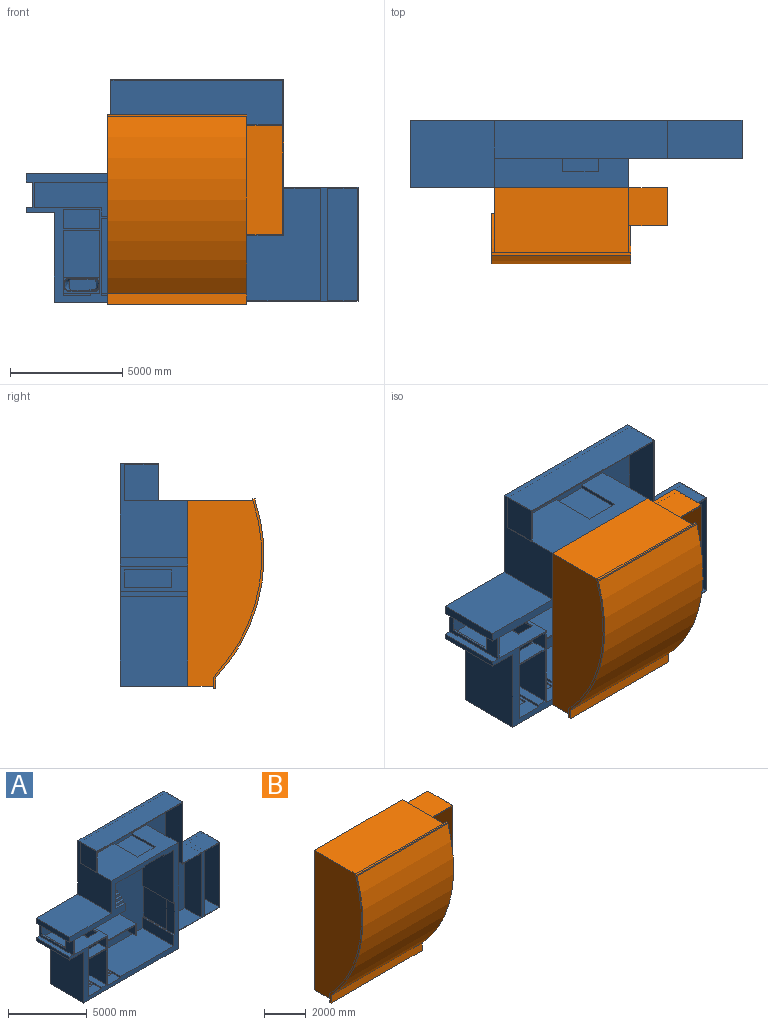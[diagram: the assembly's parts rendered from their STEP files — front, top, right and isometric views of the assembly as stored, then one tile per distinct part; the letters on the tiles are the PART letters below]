
ASSEMBLY  parts=2 mates=1
PART A: 183 faces, bbox 14773.6x3003.6x9893.6 mm
  f0: plane 2020x1630mm, normal (0,0,1), area 1096600mm2, adj f4,f10,f11,f13,f82,f112
  f1: cylinder r=5mm len=1630mm, axis (1,0,0), area 12802mm2, adj f4,f7,f11,f112
  f2: bspline ~1510x560mm, area 1818583mm2, adj f3,f5
  f3: plane 1220x470mm, normal (0,-1,0), area 564814mm2, adj f2
  f4: plane 1633.58x698.58mm, normal (0,-1,0), area 248006.1mm2, adj f0,f1,f5,f11,f112
  f5: bspline ~1556.23x596.37mm, area 160277.6mm2, adj f2,f4
  f6: plane 3000x400mm, normal (-1,0,0), area 1200000mm2, adj f13,f47,f56,f57
  f7: plane 1630x775mm, normal (0,0,1), area 1263250mm2, adj f1,f11,f27,f112
  f8: plane 1800x1220mm, normal (0,0,1), area 1096000mm2, adj f9,f13,f25,f73,f74,f75,f77
  f9: plane 1800x100mm, normal (-1,0,0), area 180000mm2, adj f8,f13,f26,f74
  f10: plane 1800x100mm, normal (-1,0,0), area 180000mm2, adj f0,f13,f39,f82
  f11: plane 2800x2790mm, normal (-1,0,0), area 7266005.4mm2, adj f0,f1,f4,f7,f12,f13,f27
  f12: plane 2800x1630mm, normal (0,0,-1), area 2674000mm2, adj f11,f13,f27,f88,f90,f91,f112
  f13: plane 9730x8240mm, normal (0,-1,0), area 13790385mm2, adj f0,f6,f8,f9,f10,f11,f12,f14
  f14: plane 2800x870mm, normal (1,0,0), area 2436000mm2, adj f13,f27,f40,f48
  f15: plane 4600x2800mm, normal (0,0,-1), area 10751500mm2, adj f13,f16,f17,f27,f113,f155
  f16: plane 2800x1130mm, normal (1,0,0), area 1484000mm2, adj f13,f15,f18,f27,f95,f96,f97
  f17: plane 2510x2475mm, normal (1,0,0), area 4446718.8mm2, adj f15,f27,f41,f139,f155,f156,f157,f158
  f18: plane 2970x2800mm, normal (0,0,1), area 6426000mm2, adj f13,f16,f19,f27,f92,f93,f94
  f19: plane 2800x400mm, normal (1,0,0), area 1120000mm2, adj f13,f18,f20,f27
  f20: plane 2800x2600mm, normal (0,0,1), area 7280000mm2, adj f13,f19,f21,f27
  f21: plane 2800x870mm, normal (1,0,0), area 2436000mm2, adj f13,f20,f22,f27
  f22: plane 2800x80mm, normal (0,0,-1), area 224000mm2, adj f13,f21,f23,f27
  f23: plane 2800x800mm, normal (-1,0,0), area 2240000mm2, adj f13,f22,f24,f27
  f24: plane 2800x2520mm, normal (0,0,-1), area 7056000mm2, adj f13,f23,f25,f27
  f25: plane 3430x2800mm, normal (1,0,0), area 9504000mm2, adj f8,f13,f24,f26,f27,f74
  f26: plane 5960x2800mm, normal (0,0,1), area 14492000mm2, adj f9,f13,f25,f27,f28,f74
  f27: plane 9131x7541mm, normal (0,-1,0), area 50748600mm2, adj f7,f11,f12,f14,f15,f16,f17,f18
  f28: plane 2800x840mm, normal (-1,0,0), area 2352000mm2, adj f13,f26,f27,f29
  f29: plane 2800x100mm, normal (0,0,1), area 280000mm2, adj f13,f27,f28,f31
  f30: plane 2800x100mm, normal (0,0,-1), area 280000mm2, adj f13,f27,f31,f34
  f31: plane 2800x2470mm, normal (-1,0,0), area 1876000mm2, adj f13,f27,f29,f30,f55,f115,f117
  f32: plane 5990x2800mm, normal (0,0,1), area 13352000mm2, adj f13,f33,f54,f58,f64,f65,f66,f68
  f33: plane 8240x3000mm, normal (1,0,0), area 17978000mm2, adj f13,f32,f53,f57,f63,f64,f71,f99
  f34: plane 4130x2800mm, normal (-1,0,0), area 11564000mm2, adj f13,f27,f30,f35
  f35: plane 2800x890mm, normal (0,0,-1), area 2492000mm2, adj f13,f27,f34,f36
  f36: plane 2800x100mm, normal (-1,0,0), area 280000mm2, adj f13,f27,f35,f38
  f37: plane 2800x100mm, normal (1,0,0), area 280000mm2, adj f13,f27,f38,f44
  f38: plane 2800x1720mm, normal (0,0,-1), area 1456000mm2, adj f13,f27,f36,f37,f69,f70,f72
  f39: plane 1800x1220mm, normal (0,0,1), area 1096000mm2, adj f10,f13,f81,f82,f84,f85,f112
  f40: plane 2800x1630mm, normal (0,0,1), area 2674000mm2, adj f13,f14,f27,f88,f90,f91,f111
  f41: plane 1818.75x1250mm, normal (0,0,-1), area 1791093.8mm2, adj f17,f27,f125,f127,f128,f129,f130,f131
  f42: plane 1100x75mm, normal (1,0,0), area 82500mm2, adj f53,f76,f80,f122
  f43: plane 1400x1240mm, normal (0,0,-1), area 376781.2mm2, adj f27,f113,f124,f125,f127,f128,f129,f130
  f44: plane 2800x2580mm, normal (0,0,-1), area 4927125mm2, adj f13,f27,f37,f46,f124,f140,f141,f142
  f45: plane 3000x1130mm, normal (-1,0,0), area 1710000mm2, adj f13,f27,f47,f49,f57,f95,f96,f97
  f46: plane 1946.25x1400mm, normal (1,0,0), area 1922375mm2, adj f13,f44,f126,f140,f169,f170,f171,f172
  f47: plane 3000x300mm, normal (0,0,-1), area 900000mm2, adj f6,f13,f45,f57
  f48: plane 2800x1630mm, normal (0,0,-1), area 2674000mm2, adj f13,f14,f27,f92,f93,f94,f111
  f49: plane 3000x300mm, normal (0,0,1), area 900000mm2, adj f13,f45,f50,f57
  f50: plane 3000x236mm, normal (-1,0,0), area 708000mm2, adj f13,f49,f51,f57
  f51: plane 3000x1260mm, normal (0,0,-1), area 3780000mm2, adj f13,f50,f52,f57
  f52: plane 3964x3000mm, normal (-1,0,0), area 11892000mm2, adj f13,f51,f53,f57
  f53: plane 8470x3000mm, normal (0,0,-1), area 23210000mm2, adj f13,f33,f42,f52,f57,f76,f79,f80
  f54: plane 4160x3000mm, normal (-1,0,0), area 7860000mm2, adj f13,f32,f56,f57,f58,f59
  f55: plane 2400x1mm, normal (0,1,0), area 2400mm2, adj f31,f78,f115,f117
  f56: plane 3740x3000mm, normal (0,0,1), area 11220000mm2, adj f6,f13,f54,f57
  f57: plane 14770x9890mm, normal (0,1,0), area 109210260mm2, adj f6,f33,f45,f47,f49,f50,f51,f52
  f58: plane 1650x1mm, normal (0,-1,0), area 1650mm2, adj f32,f54,f59,f110
  f59: plane 7720x1700mm, normal (0,0,1), area 13122500mm2, adj f54,f57,f58,f60,f99,f110
  f60: plane 4780x1700mm, normal (1,0,0), area 8126000mm2, adj f57,f59,f61,f99
  f61: plane 3310x1700mm, normal (0,0,1), area 5627000mm2, adj f57,f60,f62,f99
  f62: plane 5080x1700mm, normal (1,0,0), area 8636000mm2, adj f57,f61,f63,f99
  f63: plane 5040x1700mm, normal (0,0,-1), area 8568000mm2, adj f33,f57,f62,f99
  f64: plane 9780x9329mm, normal (0,-1,0), area 35156090mm2, adj f32,f33,f65,f67,f68,f71,f103,f105
  f65: plane 2100x150mm, normal (1,0,0), area 315000mm2, adj f32,f64,f66,f67
  f66: plane 1600x150mm, normal (0,1,0), area 240000mm2, adj f32,f65,f67,f68
  f67: plane 2100x1600mm, normal (0,0,1), area 3360000mm2, adj f64,f65,f66,f68
  f68: plane 2100x150mm, normal (-1,0,0), area 315000mm2, adj f32,f64,f66,f67
  f69: plane 2100x1mm, normal (-1,0,0), area 2100mm2, adj f27,f38,f72,f118
  f70: plane 2100x1mm, normal (1,0,0), area 2100mm2, adj f27,f38,f72,f118
  f71: plane 2100x150mm, normal (0,0,1), area 315000mm2, adj f33,f64,f114,f119
  f72: plane 1600x1mm, normal (0,1,0), area 1600mm2, adj f38,f69,f70,f118
  f73: plane 1000x75mm, normal (0,1,0), area 75000mm2, adj f8,f75,f77,f121
  f74: plane 1220x175mm, normal (0,-1,0), area 197000mm2, adj f8,f9,f25,f26,f75,f77,f121
  f75: plane 1100x75mm, normal (1,0,0), area 82500mm2, adj f8,f73,f74,f121
  f76: plane 1000x75mm, normal (0,1,0), area 75000mm2, adj f42,f53,f79,f122
  f77: plane 1100x75mm, normal (-1,0,0), area 82500mm2, adj f8,f73,f74,f121
  f78: plane 2400x2100mm, normal (-1,0,0), area 5040000mm2, adj f27,f55,f115,f117
  f79: plane 1100x75mm, normal (-1,0,0), area 82500mm2, adj f53,f76,f80,f122
  f80: plane 1000x75mm, normal (0,-1,0), area 75000mm2, adj f42,f53,f79,f122
  f81: plane 1000x75mm, normal (0,1,0), area 75000mm2, adj f39,f84,f85,f120
  f82: plane 1220x175mm, normal (0,-1,0), area 197000mm2, adj f0,f10,f39,f84,f85,f112,f120
  f83: plane 1000x75mm, normal (0,1,0), area 75000mm2, adj f53,f86,f89,f123
  f84: plane 1100x75mm, normal (-1,0,0), area 82500mm2, adj f39,f81,f82,f120
  f85: plane 1100x75mm, normal (1,0,0), area 82500mm2, adj f39,f81,f82,f120
  f86: plane 1100x75mm, normal (-1,0,0), area 82500mm2, adj f53,f83,f87,f123
  f87: plane 1000x75mm, normal (0,-1,0), area 75000mm2, adj f53,f86,f89,f123
  f88: plane 2100x70mm, normal (-1,0,0), area 147000mm2, adj f12,f27,f40,f90
  f89: plane 1100x75mm, normal (1,0,0), area 82500mm2, adj f53,f83,f87,f123
  f90: plane 900x70mm, normal (0,1,0), area 63000mm2, adj f12,f40,f88,f91
  f91: plane 2100x70mm, normal (1,0,0), area 147000mm2, adj f12,f27,f40,f90
  f92: plane 2100x70mm, normal (1,0,0), area 147000mm2, adj f18,f27,f48,f93
  f93: plane 900x70mm, normal (0,1,0), area 63000mm2, adj f18,f48,f92,f94
  f94: plane 2100x70mm, normal (-1,0,0), area 147000mm2, adj f18,f27,f48,f93
  f95: plane 800x100mm, normal (0,1,0), area 80000mm2, adj f16,f45,f96,f97
  f96: plane 2100x100mm, normal (0,0,-1), area 210000mm2, adj f16,f27,f45,f95
  f97: plane 2100x100mm, normal (0,0,1), area 210000mm2, adj f16,f27,f45,f95
  f98: plane 5000x1300mm, normal (0,-1,0), area 6500000mm2, adj f100,f101,f102,f104
  f99: plane 11029x9860mm, normal (0,-1,0), area 2698360mm2, adj f32,f33,f59,f60,f61,f62,f63,f100
  f100: plane 1500x1300mm, normal (0,0,-1), area 1950000mm2, adj f98,f99,f101,f104
  f101: plane 5000x1500mm, normal (1,0,0), area 7500000mm2, adj f98,f99,f100,f102
  f102: plane 1500x1300mm, normal (0,0,1), area 1950000mm2, adj f98,f99,f101,f104
  f103: plane 1610x1500mm, normal (1,0,0), area 2415000mm2, adj f32,f64,f99,f105
  f104: plane 5000x1500mm, normal (-1,0,0), area 7500000mm2, adj f98,f99,f100,f102
  f105: plane 7639x1500mm, normal (0,0,-1), area 11458500mm2, adj f64,f99,f103,f106
  f106: plane 4780x1500mm, normal (-1,0,0), area 7170000mm2, adj f64,f99,f105,f107
  f107: plane 1690x1500mm, normal (0,0,-1), area 2535000mm2, adj f64,f99,f106,f108
  f108: plane 5000x1500mm, normal (-1,0,0), area 7500000mm2, adj f64,f99,f107,f109
  f109: plane 3380x1500mm, normal (0,0,1), area 5070000mm2, adj f33,f64,f99,f108
  f110: plane 1650x1500mm, normal (-1,0,0), area 2475000mm2, adj f32,f58,f59,f99
  f111: plane 2800x870mm, normal (-1,0,0), area 2436000mm2, adj f13,f27,f40,f48
  f112: plane 2890x2800mm, normal (1,0,0), area 7446005.4mm2, adj f0,f1,f4,f7,f12,f13,f27,f39
  f113: plane 1710x1550mm, normal (1,0,0), area 538906.2mm2, adj f13,f15,f43,f126,f139,f155,f156,f157
  f114: plane 2400x150mm, normal (0,1,0), area 360000mm2, adj f33,f71,f116,f119
  f115: plane 2100x1mm, normal (0,0,-1), area 2100mm2, adj f27,f31,f55,f78
  f116: plane 2100x150mm, normal (0,0,-1), area 315000mm2, adj f33,f64,f114,f119
  f117: plane 2100x1mm, normal (0,0,1), area 2100mm2, adj f27,f31,f55,f78
  f118: plane 2100x1600mm, normal (0,0,-1), area 3360000mm2, adj f27,f69,f70,f72
  f119: plane 2400x2100mm, normal (1,0,0), area 5040000mm2, adj f64,f71,f114,f116
  f120: plane 1100x1000mm, normal (0,0,1), area 1100000mm2, adj f81,f82,f84,f85
  f121: plane 1100x1000mm, normal (0,0,1), area 1100000mm2, adj f73,f74,f75,f77
  f122: plane 1100x1000mm, normal (0,0,-1), area 1100000mm2, adj f42,f76,f79,f80
  f123: plane 1100x1000mm, normal (0,0,-1), area 1100000mm2, adj f83,f86,f87,f89
  f124: plane 800x175mm, normal (1,0,0), area 140000mm2, adj f27,f43,f44,f154
  f125: plane 800x200mm, normal (-1,0,0), area 160000mm2, adj f27,f41,f43,f127
  f126: plane 860x175mm, normal (0,0,1), area 150500mm2, adj f13,f46,f113,f182
  f127: plane 800x131.25mm, normal (0,1,0), area 105000mm2, adj f41,f43,f125,f128
  f128: plane 800x175mm, normal (-1,0,0), area 140000mm2, adj f41,f43,f127,f129
  f129: plane 800x131.25mm, normal (0,1,0), area 105000mm2, adj f41,f43,f128,f130
  f130: plane 800x175mm, normal (-1,0,0), area 140000mm2, adj f41,f43,f129,f131
  f131: plane 800x131.25mm, normal (0,1,0), area 105000mm2, adj f41,f43,f130,f132
  f132: plane 800x175mm, normal (-1,0,0), area 140000mm2, adj f41,f43,f131,f133
  f133: plane 800x131.25mm, normal (0,1,0), area 105000mm2, adj f41,f43,f132,f134
  f134: plane 800x175mm, normal (-1,0,0), area 140000mm2, adj f41,f43,f133,f135
  f135: plane 800x131.25mm, normal (0,1,0), area 105000mm2, adj f41,f43,f134,f136
  f136: plane 800x175mm, normal (-1,0,0), area 140000mm2, adj f41,f43,f135,f137
  f137: plane 800x131.25mm, normal (0,1,0), area 105000mm2, adj f41,f43,f136,f138
  f138: plane 800x175mm, normal (-1,0,0), area 140000mm2, adj f41,f43,f137,f139
  f139: plane 1031.25x950mm, normal (0,1,0), area 954000mm2, adj f17,f41,f43,f113,f138,f168
  f140: plane 1181.25x800mm, normal (0,-1,0), area 945000mm2, adj f43,f44,f46,f141,f169
  f141: plane 800x175mm, normal (1,0,0), area 140000mm2, adj f43,f44,f140,f142
  f142: plane 800x131.25mm, normal (0,-1,0), area 105000mm2, adj f43,f44,f141,f143
  f143: plane 800x175mm, normal (1,0,0), area 140000mm2, adj f43,f44,f142,f144
  f144: plane 800x131.25mm, normal (0,-1,0), area 105000mm2, adj f43,f44,f143,f145
  f145: plane 800x175mm, normal (1,0,0), area 140000mm2, adj f43,f44,f144,f146
  f146: plane 800x131.25mm, normal (0,-1,0), area 105000mm2, adj f43,f44,f145,f147
  f147: plane 800x175mm, normal (1,0,0), area 140000mm2, adj f43,f44,f146,f148
  f148: plane 800x131.25mm, normal (0,-1,0), area 105000mm2, adj f43,f44,f147,f149
  f149: plane 800x175mm, normal (1,0,0), area 140000mm2, adj f43,f44,f148,f150
  f150: plane 800x131.25mm, normal (0,-1,0), area 105000mm2, adj f43,f44,f149,f151
  f151: plane 800x175mm, normal (1,0,0), area 140000mm2, adj f43,f44,f150,f152
  f152: plane 800x131.25mm, normal (0,-1,0), area 105000mm2, adj f43,f44,f151,f153
  f153: plane 800x175mm, normal (1,0,0), area 140000mm2, adj f43,f44,f152,f154
  f154: plane 800x131.25mm, normal (0,-1,0), area 105000mm2, adj f43,f44,f124,f153
  f155: plane 860x577.5mm, normal (0,1,0), area 496650mm2, adj f15,f17,f113,f156
  f156: plane 860x175mm, normal (0,0,-1), area 150500mm2, adj f17,f113,f155,f157
  f157: plane 860x163.75mm, normal (0,1,0), area 140825mm2, adj f17,f113,f156,f158
  f158: plane 860x175mm, normal (0,0,-1), area 150500mm2, adj f17,f113,f157,f159
  f159: plane 860x163.75mm, normal (0,1,0), area 140825mm2, adj f17,f113,f158,f160
  f160: plane 860x175mm, normal (0,0,-1), area 150500mm2, adj f17,f113,f159,f161
  f161: plane 860x163.75mm, normal (0,1,0), area 140825mm2, adj f17,f113,f160,f162
  f162: plane 860x175mm, normal (0,0,-1), area 150500mm2, adj f17,f113,f161,f163
  f163: plane 860x163.75mm, normal (0,1,0), area 140825mm2, adj f17,f113,f162,f164
  f164: plane 860x175mm, normal (0,0,-1), area 150500mm2, adj f17,f113,f163,f165
  f165: plane 860x163.75mm, normal (0,1,0), area 140825mm2, adj f17,f113,f164,f166
  f166: plane 860x175mm, normal (0,0,-1), area 150500mm2, adj f17,f113,f165,f167
  f167: plane 860x163.75mm, normal (0,1,0), area 140825mm2, adj f17,f113,f166,f168
  f168: plane 860x175mm, normal (0,0,-1), area 150500mm2, adj f17,f113,f139,f167
  f169: plane 860x175mm, normal (0,0,1), area 150500mm2, adj f46,f113,f140,f170
  f170: plane 860x163.75mm, normal (0,-1,0), area 140825mm2, adj f46,f113,f169,f171
  f171: plane 860x175mm, normal (0,0,1), area 150500mm2, adj f46,f113,f170,f172
  f172: plane 860x163.75mm, normal (0,-1,0), area 140825mm2, adj f46,f113,f171,f173
  f173: plane 860x175mm, normal (0,0,1), area 150500mm2, adj f46,f113,f172,f174
  f174: plane 860x163.75mm, normal (0,-1,0), area 140825mm2, adj f46,f113,f173,f175
  f175: plane 860x175mm, normal (0,0,1), area 150500mm2, adj f46,f113,f174,f176
  f176: plane 860x163.75mm, normal (0,-1,0), area 140825mm2, adj f46,f113,f175,f177
  f177: plane 860x175mm, normal (0,0,1), area 150500mm2, adj f46,f113,f176,f178
  f178: plane 860x163.75mm, normal (0,-1,0), area 140825mm2, adj f46,f113,f177,f179
  f179: plane 860x175mm, normal (0,0,1), area 150500mm2, adj f46,f113,f178,f180
  f180: plane 860x163.75mm, normal (0,-1,0), area 140825mm2, adj f46,f113,f179,f181
  f181: plane 860x175mm, normal (0,0,1), area 150500mm2, adj f46,f113,f180,f182
  f182: plane 860x163.75mm, normal (0,-1,0), area 140825mm2, adj f46,f113,f126,f181
PART B: 133 faces, bbox 7820x3403.7x8440 mm
  f0: plane 2802.57x1980mm, normal (0,0,-1), area 3537610.9mm2, adj f15,f28,f29,f47,f50,f54,f86,f87
  f1: plane 8240x3303.73mm, normal (-1,0,0), area 22415522.4mm2, adj f2,f7,f13,f21,f22
  f2: cylinder r=7819.43mm len=7840mm, axis (-1,0,0), area 843864.5mm2, adj f1,f3,f4,f7
  f3: plane 8440x2253.73mm, normal (-1,0,0), area 903273.3mm2, adj f2,f4,f7,f8,f9,f64,f65,f66
  f4: plane 6190x100mm, normal (0,1,0), area 619000mm2, adj f2,f3,f9,f10,f11,f22
  f5: cylinder r=7801.32mm len=4420mm, axis (-1,0,0), area 606847.5mm2, adj f6,f34,f36,f124
  f6: plane 4420x2543.43mm, normal (1,0,0), area 1987987.9mm2, adj f5,f34,f36,f59
  f7: plane 6190x500mm, normal (0,1,0), area 699000mm2, adj f1,f2,f3,f10,f11,f12,f13,f64
  f8: plane 6190x68.66mm, normal (0,-1,0), area 424988.9mm2, adj f3,f9,f10,f66
  f9: plane 6190x94.96mm, normal (0,0,1), area 587810.1mm2, adj f3,f4,f8,f10
  f10: plane 8440x2253.73mm, normal (1,0,0), area 903273.3mm2, adj f4,f7,f8,f9,f11,f64,f65,f66
  f11: cylinder r=7819.43mm len=7840mm, axis (-1,0,0), area 843864.5mm2, adj f4,f7,f10,f12
  f12: plane 8240x3303.73mm, normal (1,0,0), area 16446946.2mm2, adj f7,f11,f13,f18,f19,f21,f22,f27
  f13: plane 5990x1150mm, normal (0,0,-1), area 6888500mm2, adj f1,f7,f12,f21
  f14: plane 3043.43x1720mm, normal (0,0,-1), area 3234695.9mm2, adj f15,f16,f23,f48,f53,f55,f70,f84
  f15: plane 7440x5291mm, normal (0,-1,0), area 36171450.5mm2, adj f0,f14,f16,f17,f23,f24,f25,f26
  f16: plane 3303.73x3020mm, normal (-1,0,0), area 9590015.2mm2, adj f14,f15,f17,f21,f40,f55
  f17: plane 860x200mm, normal (0,0,1), area 172000mm2, adj f15,f16,f21,f30
  f18: plane 1730x1700mm, normal (0,0,1), area 2941000mm2, adj f12,f19,f20,f21
  f19: plane 4920x1730mm, normal (0,-1,0), area 332000mm2, adj f12,f18,f20,f27,f67,f68,f69
  f20: plane 4920x1700mm, normal (1,0,0), area 8364000mm2, adj f18,f19,f21,f27
  f21: plane 8240x7720mm, normal (0,1,0), area 56054600mm2, adj f1,f12,f13,f16,f17,f18,f20,f22
  f22: plane 5990x2909.73mm, normal (0,0,1), area 17429252.4mm2, adj f1,f4,f12,f21
  f23: plane 3043.43x1100mm, normal (-1,0,0), area 1352684.1mm2, adj f14,f15,f26,f48,f89,f90,f91
  f24: plane 4420x3043.43mm, normal (-1,0,0), area 7522535.5mm2, adj f15,f34,f36,f60,f95,f96,f97
  f25: plane 1980x950mm, normal (0,0,1), area 1759500mm2, adj f15,f28,f29,f47,f50,f54,f98,f105
  f26: plane 2824.98x2580mm, normal (0,0,1), area 5240959.8mm2, adj f15,f23,f30,f48,f53,f55,f86,f87
  f27: plane 1730x1700mm, normal (0,0,-1), area 2941000mm2, adj f12,f19,f20,f21
  f28: plane 3240x2352.62mm, normal (-1,0,0), area 5186439.9mm2, adj f0,f15,f25,f47
  f29: plane 3240x2352.62mm, normal (1,0,0), area 5186439.9mm2, adj f0,f15,f25,f114
  f30: plane 4120x2851.88mm, normal (1,0,0), area 10970211mm2, adj f15,f17,f21,f26,f40,f116
  f31: plane 3043.43x1180mm, normal (1,0,0), area 1577792.6mm2, adj f15,f32,f34,f56,f89,f90,f91
  f32: plane 2802.57x600mm, normal (0,0,-1), area 1681544.7mm2, adj f15,f31,f37,f56
  f33: plane 3103.73x2940mm, normal (-1,0,0), area 5312152.1mm2, adj f15,f35,f39,f61,f92,f93,f94
  f34: plane 3043.43x2530mm, normal (0,0,-1), area 7534872.2mm2, adj f5,f6,f15,f24,f31,f56,f58,f59
  f35: plane 4250x2830mm, normal (0,0,-1), area 11749940.5mm2, adj f15,f33,f38,f49,f51,f52,f57,f61
  f36: plane 3130x950mm, normal (0,0,1), area 2808800mm2, adj f5,f6,f15,f24,f37,f56,f58,f59
  f37: plane 3240x2802.57mm, normal (1,0,0), area 6642992.9mm2, adj f15,f32,f36,f56
  f38: plane 3103.73x2940mm, normal (1,0,0), area 8924152.1mm2, adj f15,f35,f39,f51
  f39: plane 4250x3053.01mm, normal (0,0,1), area 10810214.3mm2, adj f15,f33,f38,f49,f51,f52,f57,f61
  f40: plane 3030x860mm, normal (0,0,-1), area 2557568.3mm2, adj f16,f21,f30,f55,f116,f117
  f41: plane 4840x1840mm, normal (0,-1,0), area 8562168.8mm2, adj f12,f44,f46,f67,f68,f69,f73,f75
  f42: plane 1907.33x1520mm, normal (-1,0,0), area 2899147.4mm2, adj f15,f77,f79,f81
  f43: plane 1907.33x1030.46mm, normal (-1,0,0), area 1965428.8mm2, adj f15,f72,f74,f76
  f44: plane 1907.33x1520mm, normal (1,0,0), area 2899147.4mm2, adj f41,f78,f80,f82
  f45: plane 2100x1235mm, normal (-1,0,0), area 622821.2mm2, adj f15,f72,f74,f76,f95,f96,f97
  f46: plane 1907.33x1030.46mm, normal (1,0,0), area 1965428.8mm2, adj f41,f71,f73,f75
  f47: cylinder r=7801.32mm len=3240mm, axis (-1,0,0), area 158290mm2, adj f0,f25,f28,f98
  f48: cylinder r=7819.43mm len=1100mm, axis (-1,0,0), area 583671mm2, adj f14,f23,f26,f104
  f49: cylinder r=7819.43mm len=2940mm, axis (-1,0,0), area 2536099.3mm2, adj f35,f39,f122,f126
  f50: cylinder r=7819.43mm len=3240mm, axis (-1,0,0), area 3222161.9mm2, adj f0,f25,f98,f106
  f51: cylinder r=7819.43mm len=2940mm, axis (-1,0,0), area 62290.2mm2, adj f35,f38,f39,f108
  f52: cylinder r=7819.43mm len=2940mm, axis (-1,0,0), area 2536099.3mm2, adj f35,f39,f102,f111
  f53: cylinder r=7819.43mm len=1100mm, axis (-1,0,0), area 959689.8mm2, adj f14,f26,f103,f110
  f54: cylinder r=7819.43mm len=3240mm, axis (-1,0,0), area 3222161.9mm2, adj f0,f25,f105,f115
  f55: cylinder r=7819.43mm len=4120mm, axis (-1,0,0), area 3256953.9mm2, adj f14,f16,f26,f40,f107,f117
  f56: cylinder r=7819.43mm len=4420mm, axis (-1,0,0), area 3529570.6mm2, adj f31,f32,f34,f36,f37,f118
  f57: cylinder r=7819.43mm len=2940mm, axis (-1,0,0), area 2536099.3mm2, adj f35,f39,f101,f120
  f58: cylinder r=7819.43mm len=4420mm, axis (-1,0,0), area 4252885mm2, adj f34,f36,f119,f124
  f59: cylinder r=7819.43mm len=4420mm, axis (-1,0,0), area 4252885mm2, adj f6,f34,f36,f128
  f60: cylinder r=7819.43mm len=4420mm, axis (-1,0,0), area 989852.8mm2, adj f24,f34,f36,f129
  f61: cylinder r=7819.43mm len=2940mm, axis (-1,0,0), area 590273.4mm2, adj f33,f35,f39,f131
  f62: cylinder r=7819.43mm len=2940mm, axis (-1,0,0), area 2536099.3mm2, adj f35,f39,f63,f125
  f63: plane 2940x728.74mm, normal (-1,0,0), area 1330980.9mm2, adj f35,f39,f62,f132
  f64: plane 6190x100mm, normal (0,0,-1), area 619000mm2, adj f3,f7,f10,f65
  f65: plane 6190x460.18mm, normal (0,-1,0), area 2848534mm2, adj f3,f10,f64,f66
  f66: cylinder r=7919.43mm len=7911.16mm, axis (-1,0,0), area 52655193mm2, adj f3,f8,f10,f65
  f67: plane 1690x1500mm, normal (0,0,-1), area 2535000mm2, adj f12,f19,f41,f68
  f68: plane 4840x1500mm, normal (-1,0,0), area 7260000mm2, adj f19,f41,f67,f69
  f69: plane 1690x1500mm, normal (0,0,1), area 2535000mm2, adj f12,f19,f41,f68
  f70: plane 900x80mm, normal (0,1,0), area 72000mm2, adj f14,f39,f84,f85
  f71: plane 1030.46x150mm, normal (0,1,0), area 154568.8mm2, adj f12,f46,f73,f75
  f72: plane 1030.46x1mm, normal (0,1,0), area 1030.5mm2, adj f43,f45,f74,f76
  f73: plane 1907.33x150mm, normal (0,0,-1), area 286100.1mm2, adj f12,f41,f46,f71
  f74: plane 1907.33x1mm, normal (0,0,-1), area 1907.3mm2, adj f15,f43,f45,f72
  f75: plane 1907.33x150mm, normal (0,0,1), area 286100.1mm2, adj f12,f41,f46,f71
  f76: plane 1907.33x1mm, normal (0,0,1), area 1907.3mm2, adj f15,f43,f45,f72
  f77: plane 1907.33x1mm, normal (0,0,-1), area 1907.3mm2, adj f15,f42,f79,f83
  f78: plane 1907.33x150mm, normal (0,0,-1), area 286100.1mm2, adj f12,f41,f44,f80
  f79: plane 1520x1mm, normal (0,1,0), area 1520mm2, adj f42,f77,f81,f83
  f80: plane 1520x150mm, normal (0,1,0), area 228000mm2, adj f12,f44,f78,f82
  f81: plane 1907.33x1mm, normal (0,0,1), area 1907.3mm2, adj f15,f42,f79,f83
  f82: plane 1907.33x150mm, normal (0,0,1), area 286100.1mm2, adj f12,f41,f44,f80
  f83: plane 2100x1720mm, normal (-1,0,0), area 712852.6mm2, adj f15,f77,f79,f81,f92,f93,f94
  f84: plane 2100x80mm, normal (-1,0,0), area 168000mm2, adj f14,f15,f39,f70
  f85: plane 2100x80mm, normal (1,0,0), area 168000mm2, adj f14,f15,f39,f70
  f86: plane 2100x80mm, normal (1,0,0), area 168000mm2, adj f0,f15,f26,f88
  f87: plane 2100x80mm, normal (-1,0,0), area 168000mm2, adj f0,f15,f26,f88
  f88: plane 900x80mm, normal (0,1,0), area 72000mm2, adj f0,f26,f86,f87
  f89: plane 900x80mm, normal (0,1,0), area 72000mm2, adj f23,f31,f90,f91
  f90: plane 2100x80mm, normal (0,0,1), area 168000mm2, adj f15,f23,f31,f89
  f91: plane 2100x80mm, normal (0,0,-1), area 168000mm2, adj f15,f23,f31,f89
  f92: plane 2100x100mm, normal (0,0,1), area 210000mm2, adj f15,f33,f83,f93
  f93: plane 1720x100mm, normal (0,1,0), area 172000mm2, adj f33,f83,f92,f94
  f94: plane 2100x100mm, normal (0,0,-1), area 210000mm2, adj f15,f33,f83,f93
  f95: plane 2100x100mm, normal (0,0,-1), area 210000.6mm2, adj f15,f24,f45,f96
  f96: plane 1230x100mm, normal (0,1,0), area 123000mm2, adj f24,f45,f95,f97
  f97: plane 2100x100mm, normal (0,0,1), area 210000mm2, adj f15,f24,f45,f96
  f98: plane 3240x2302.57mm, normal (-1,0,0), area 1456553mm2, adj f0,f25,f47,f50
  f99: cylinder r=7801.32mm len=1100mm, axis (-1,0,0), area 136918.6mm2, adj f14,f26,f103,f104
  f100: cylinder r=7801.32mm len=2940mm, axis (-1,0,0), area 361925.2mm2, adj f35,f39,f101,f102
  f101: plane 2940x728.74mm, normal (1,0,0), area 1330980.9mm2, adj f35,f39,f57,f100
  f102: plane 2940x728.74mm, normal (-1,0,0), area 1330980.9mm2, adj f35,f39,f52,f100
  f103: plane 1100x668.45mm, normal (-1,0,0), area 495436.8mm2, adj f14,f26,f53,f99
  f104: plane 1100x668.45mm, normal (1,0,0), area 495436.8mm2, adj f14,f26,f48,f99
  f105: plane 3240x2302.57mm, normal (-1,0,0), area 1456553mm2, adj f0,f25,f54,f109
  f106: plane 3240x2302.57mm, normal (1,0,0), area 1456553mm2, adj f0,f25,f50,f109
  f107: plane 1100x668.45mm, normal (-1,0,0), area 495436.8mm2, adj f14,f26,f55,f112
  f108: plane 2940x728.74mm, normal (-1,0,0), area 1330980.9mm2, adj f35,f39,f51,f113
  f109: cylinder r=7801.32mm len=3240mm, axis (1,0,0), area 459794.7mm2, adj f0,f25,f105,f106
  f110: plane 1100x668.45mm, normal (1,0,0), area 495436.8mm2, adj f14,f26,f53,f112
  f111: plane 2940x728.74mm, normal (1,0,0), area 1330980.9mm2, adj f35,f39,f52,f113
  f112: cylinder r=7801.32mm len=1100mm, axis (1,0,0), area 136918.6mm2, adj f14,f26,f107,f110
  f113: cylinder r=7801.32mm len=2940mm, axis (1,0,0), area 361925.2mm2, adj f35,f39,f108,f111
  f114: cylinder r=7801.32mm len=3240mm, axis (-1,0,0), area 399493.8mm2, adj f0,f25,f29,f115
  f115: plane 3240x2302.57mm, normal (1,0,0), area 1456553mm2, adj f0,f25,f54,f114
  f116: cylinder r=7801.32mm len=4120mm, axis (-1,0,0), area 441961.3mm2, adj f26,f30,f40,f117
  f117: plane 4120x728.74mm, normal (1,0,0), area 1862488.3mm2, adj f26,f40,f55,f116
  f118: plane 4420x2543.43mm, normal (-1,0,0), area 1987987.9mm2, adj f34,f36,f56,f121
  f119: plane 4420x2543.43mm, normal (1,0,0), area 1987987.9mm2, adj f34,f36,f58,f121
  f120: plane 2940x728.74mm, normal (-1,0,0), area 1330980.9mm2, adj f35,f39,f57,f123
  f121: cylinder r=7801.32mm len=4420mm, axis (1,0,0), area 606847.5mm2, adj f34,f36,f118,f119
  f122: plane 2940x728.74mm, normal (1,0,0), area 1330980.9mm2, adj f35,f39,f49,f123
  f123: cylinder r=7801.32mm len=2940mm, axis (1,0,0), area 361925.2mm2, adj f35,f39,f120,f122
  f124: plane 4420x2543.43mm, normal (-1,0,0), area 1987987.9mm2, adj f5,f34,f36,f58
  f125: plane 2940x728.74mm, normal (1,0,0), area 1330980.9mm2, adj f35,f39,f62,f127
  f126: plane 2940x728.74mm, normal (-1,0,0), area 1330980.9mm2, adj f35,f39,f49,f127
  f127: cylinder r=7801.32mm len=2940mm, axis (-1,0,0), area 361925.2mm2, adj f35,f39,f125,f126
  f128: plane 4420x2543.43mm, normal (-1,0,0), area 1987987.9mm2, adj f34,f36,f59,f130
  f129: plane 4420x2543.43mm, normal (1,0,0), area 1987987.9mm2, adj f34,f36,f60,f130
  f130: cylinder r=7801.32mm len=4420mm, axis (1,0,0), area 606847.5mm2, adj f34,f36,f128,f129
  f131: plane 2940x728.74mm, normal (1,0,0), area 1330980.9mm2, adj f35,f39,f61,f132
  f132: cylinder r=7801.32mm len=2940mm, axis (1,0,0), area 361925.2mm2, adj f35,f39,f63,f131
PLACE A t=(-1830,0,4140)mm
PLACE B t=(-1830,0,4140)mm
MATE fastened B.f21 <-> A.f13  axis (0,1,0) through (3760,-2800,4440)mm
